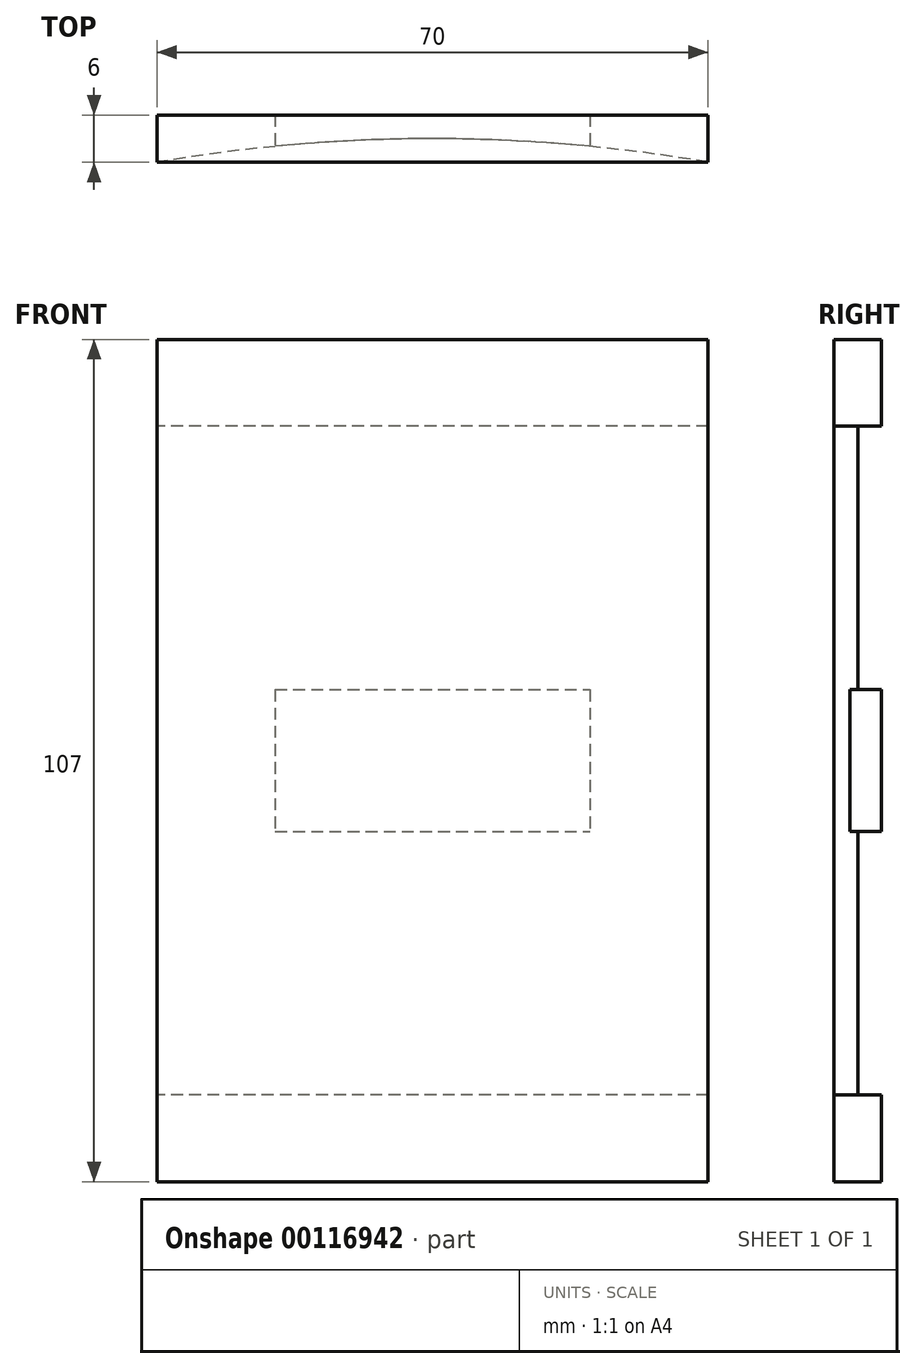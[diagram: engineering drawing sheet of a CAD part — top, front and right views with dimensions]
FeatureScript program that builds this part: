
annotation { "Feature Type Name" : "Feature", "Feature Type Description" : "" }
export const myFeature = defineFeature(function(context is Context, id is Id, definition is map)
    precondition{}
    {
        {
            var Q0;
            Q0=qCreatedBy(makeId("Top.planeOp"),FACE);
            var sketch = newSketch(context, id + "F0", { "sketchPlane" : qUnion([Q0])});
            skArc(sketch, "E0", {"start": v(70, 0) * mm, "mid": v(35, 3) * mm, "end": v(0, 0) * mm});
            skLineSegment(sketch, "E1", {"start": v(0, 0) * mm, "end": v(70, 0) * mm});
            skSolve(sketch);
        }
        {
            var Q0;
            Q0=makeQuery(id+"F0.imprint","IMPRINT",FACE,{"disambiguationData":[TD([[makeQuery(id+"F0.imprint","IMPRINT",EDGE,{"derivedFrom":sQuery(id+"F0.wireOp",EDGE,"E0")}),1.0]])]});
            extrude(context, id + "F1", {"entities" : qUnion([Q0]), "depth" : 107 * mm});
        }
        {
            var Q0;
            Q0=makeQuery(id+"F1.opExtrude","SWEPT_FACE",FACE,{"disambiguationData":[OSD([sQuery(id+"F0.wireOp",EDGE,"E1")])]});
            var sketch = newSketch(context, id + "F2", { "sketchPlane" : qUnion([Q0])});
            skLineSegment(sketch, "E2.bottom", {"start": v(70, 107) * mm, "end": v(0, 107) * mm});
            skLineSegment(sketch, "E2.top", {"start": v(70, 96) * mm, "end": v(0, 96) * mm});
            skLineSegment(sketch, "E2.left", {"start": v(70, 107) * mm, "end": v(70, 96) * mm});
            skLineSegment(sketch, "E2.right", {"start": v(0, 107) * mm, "end": v(0, 96) * mm});
            skLineSegment(sketch, "E3.bottom", {"start": v(70, 0) * mm, "end": v(0, 0) * mm});
            skLineSegment(sketch, "E3.top", {"start": v(70, 11) * mm, "end": v(0, 11) * mm});
            skLineSegment(sketch, "E3.left", {"start": v(70, 0) * mm, "end": v(70, 11) * mm});
            skLineSegment(sketch, "E3.right", {"start": v(0, 0) * mm, "end": v(0, 11) * mm});
            skLineSegment(sketch, "E4", {"start": v(70, 53.5) * mm, "end": v(0, 53.5) * mm, "construction": true});
            skLineSegment(sketch, "E5.bottom", {"start": v(15, 62.5) * mm, "end": v(55, 62.5) * mm});
            skLineSegment(sketch, "E5.top", {"start": v(15, 44.5) * mm, "end": v(55, 44.5) * mm});
            skLineSegment(sketch, "E5.left", {"start": v(15, 62.5) * mm, "end": v(15, 44.5) * mm});
            skLineSegment(sketch, "E5.right", {"start": v(55, 62.5) * mm, "end": v(55, 44.5) * mm});
            skPoint(sketch, "E6", {"position": v(55, 53.5) * mm});
            skPoint(sketch, "E7", {"position": v(35, 62.5) * mm});
            skPoint(sketch, "E8", {"position": v(35, 53.5) * mm});
            skSolve(sketch);
        }
        {
            var Q0;
            Q0=makeQuery(id+"F2.imprint","IMPRINT",FACE,{"disambiguationData":[TD([[makeQuery(id+"F2.imprint","IMPRINT",EDGE,{"derivedFrom":sQuery(id+"F2.wireOp",EDGE,"E2.bottom")}),-1.0]])]});
            var Q1;
            Q1=makeQuery(id+"F2.imprint","IMPRINT",FACE,{"disambiguationData":[TD([[makeQuery(id+"F2.imprint","IMPRINT",EDGE,{"derivedFrom":sQuery(id+"F2.wireOp",EDGE,"E5.bottom")}),-1.0]])]});
            var Q2;
            Q2=makeQuery(id+"F2.imprint","IMPRINT",FACE,{"disambiguationData":[TD([[makeQuery(id+"F2.imprint","IMPRINT",EDGE,{"derivedFrom":sQuery(id+"F2.wireOp",EDGE,"E3.bottom")}),1.0]])]});
            extrude(context, id + "F3", {"entities" : qUnion([Q0, Q1, Q2]), "operationType" : NewBodyOperationType.ADD, "oppositeDirection" : true, "depth" : 6 * mm});
        }
    });
